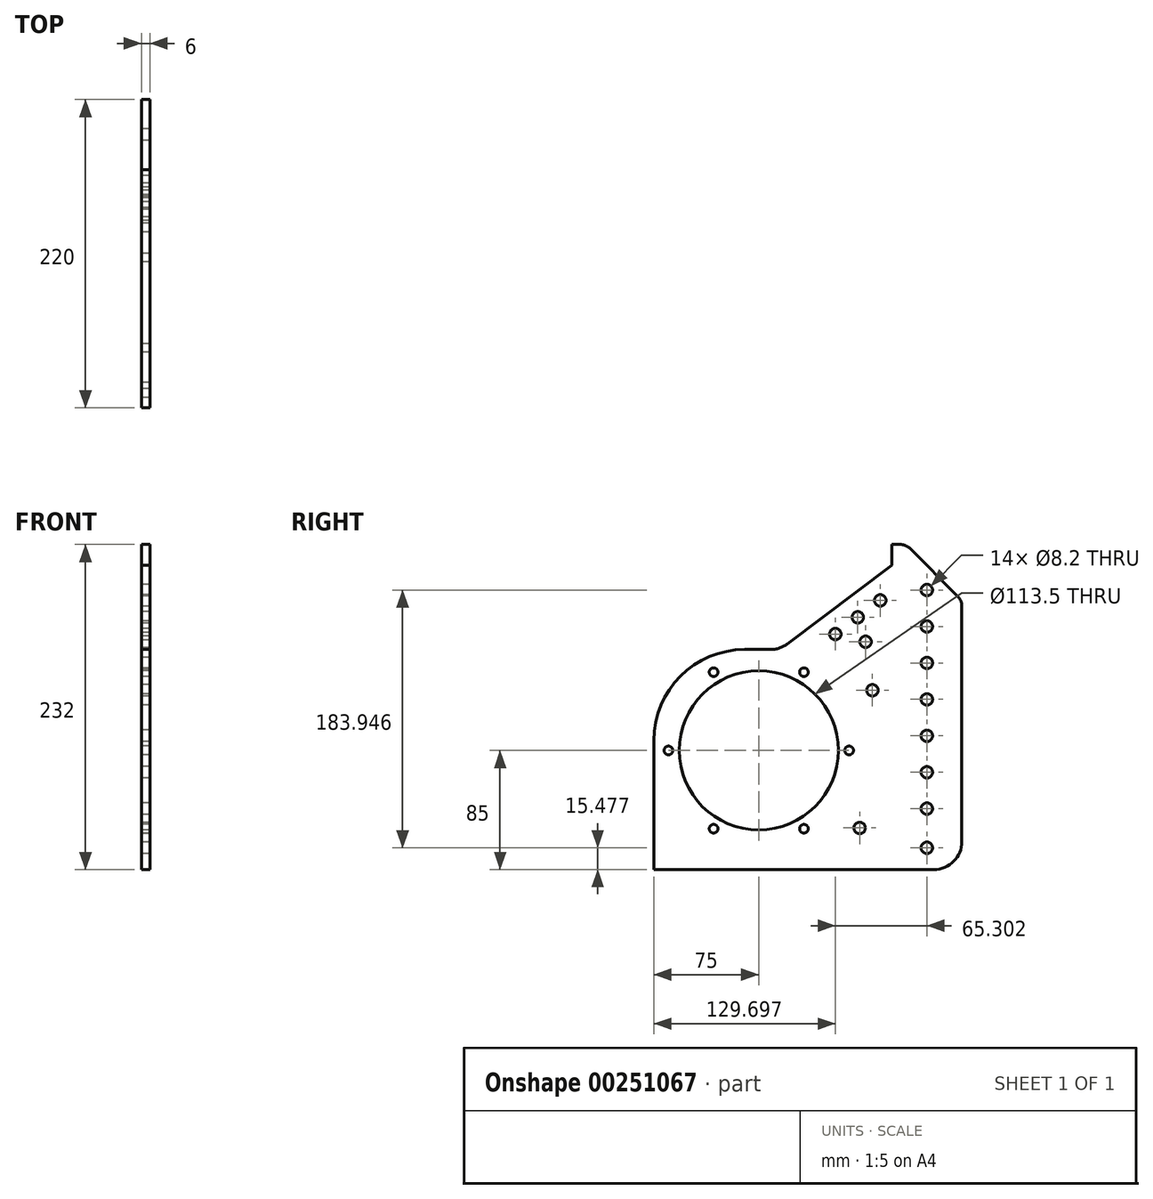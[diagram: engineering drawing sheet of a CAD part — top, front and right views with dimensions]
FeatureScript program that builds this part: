
annotation { "Feature Type Name" : "Feature", "Feature Type Description" : "" }
export const myFeature = defineFeature(function(context is Context, id is Id, definition is map)
    precondition{}
    {
        {
            var Q0;
            Q0=qCreatedBy(makeId("Right.planeOp"),FACE);
            var sketch = newSketch(context, id + "F0", { "sketchPlane" : qUnion([Q0])});
            skLineSegment(sketch, "E0.bottom", {"start": v(-20, 0) * mm, "end": v(-220, 0) * mm});
            skLineSegment(sketch, "E0.left", {"start": v(0, 20) * mm, "end": v(0, 187.86) * mm});
            skLineSegment(sketch, "E0.right", {"start": v(-220, 0) * mm, "end": v(-220, 92) * mm});
            skCircle(sketch, "E1", {"center": v(-145, 85) * mm, "radius": 56.75 * mm});
            skCircle(sketch, "E2", {"center": v(-145, 85) * mm, "radius": 64.5 * mm, "construction": true});
            skCircle(sketch, "E3", {"center": v(-80.5, 85) * mm, "radius": 3.1 * mm});
            skLineSegment(sketch, "E4", {"start": v(25.99, 85) * mm, "end": v(-259.94, 85) * mm, "construction": true});
            skCircle(sketch, "E5.1.0", {"center": v(-112.75, 140.86) * mm, "radius": 3.1 * mm});
            skCircle(sketch, "E5.2.0", {"center": v(-177.25, 140.86) * mm, "radius": 3.1 * mm});
            skCircle(sketch, "E5.3.0", {"center": v(-209.5, 85) * mm, "radius": 3.1 * mm});
            skCircle(sketch, "E5.4.0", {"center": v(-177.25, 29.14) * mm, "radius": 3.1 * mm});
            skCircle(sketch, "E5.5.0", {"center": v(-112.75, 29.14) * mm, "radius": 3.1 * mm});
            skCircle(sketch, "E6", {"center": v(-145, 85) * mm, "radius": 55 * mm, "construction": true});
            skCircle(sketch, "E7", {"center": v(-145, 85) * mm, "radius": 42.5 * mm, "construction": true});
            skLineSegment(sketch, "E8", {"start": v(-25, -2.5) * mm, "end": v(-25, 245.05) * mm, "construction": true});
            skLineSegment(sketch, "E9.top", {"start": v(-44.14, 232) * mm, "end": v(-50, 232) * mm});
            skLineSegment(sketch, "E9.right", {"start": v(-50, 157) * mm, "end": v(-50, 232) * mm});
            skCircle(sketch, "E10", {"center": v(-25, 199.42) * mm, "radius": 26 * mm, "construction": true});
            skCircle(sketch, "E11", {"center": v(-25, 199.42) * mm, "radius": 4.1 * mm});
            skLineSegment(sketch, "E12", {"start": v(-136.67, 157) * mm, "end": v(-155, 157) * mm});
            skLineSegment(sketch, "E13.bottom", {"start": v(-50, 232) * mm, "end": v(-44, 232) * mm, "construction": true});
            skLineSegment(sketch, "E13.top", {"start": v(-50, 0) * mm, "end": v(-44, 0) * mm, "construction": true});
            skLineSegment(sketch, "E13.left", {"start": v(-50, 232) * mm, "end": v(-50, 0) * mm, "construction": true});
            skLineSegment(sketch, "E13.right", {"start": v(-44, 232) * mm, "end": v(-44, 0) * mm, "construction": true});
            skCircle(sketch, "E14.0.1.0", {"center": v(-25, 173.42) * mm, "radius": 4.1 * mm});
            skCircle(sketch, "E14.0.2.0", {"center": v(-25, 147.42) * mm, "radius": 4.1 * mm});
            skCircle(sketch, "E14.0.3.0", {"center": v(-25, 121.42) * mm, "radius": 4.1 * mm});
            skCircle(sketch, "E14.0.4.0", {"center": v(-25, 95.42) * mm, "radius": 4.1 * mm});
            skCircle(sketch, "E14.0.5.0", {"center": v(-25, 69.42) * mm, "radius": 4.1 * mm});
            skCircle(sketch, "E14.0.6.0", {"center": v(-25, 43.42) * mm, "radius": 4.1 * mm});
            skCircle(sketch, "E14.0.7.0", {"center": v(-25, 15.48) * mm, "radius": 4.1 * mm});
            skLineSegment(sketch, "E14.direction2", {"start": v(-25, 199.42) * mm, "end": v(-25, 173.42) * mm, "construction": true});
            skPoint(sketch, "E15.visualSharp", {"position": v(0, 232) * mm});
            skPoint(sketch, "E16.visualSharp", {"position": v(0, 0) * mm});
            skArc(sketch, "E16.filletArc", {"start": v(-20, 0) * mm, "mid": v(-5.86, 5.86) * mm, "end": v(0, 20) * mm});
            skPoint(sketch, "E17.visualSharp", {"position": v(-220, 157) * mm});
            skArc(sketch, "E17.filletArc", {"start": v(-155, 157) * mm, "mid": v(-200.96, 137.96) * mm, "end": v(-220, 92) * mm});
            skPoint(sketch, "E18.visualSharp", {"position": v(-220, 0) * mm});
            skCircle(sketch, "E19", {"center": v(-72.99, 29.66) * mm, "radius": 4.1 * mm});
            skCircle(sketch, "E20", {"center": v(-63.87, 127.94) * mm, "radius": 4.1 * mm});
            skCircle(sketch, "E21", {"center": v(-63.87, 127.94) * mm, "radius": 20 * mm, "construction": true});
            skCircle(sketch, "E22", {"center": v(-72.99, 29.66) * mm, "radius": 26 * mm, "construction": true});
            skCircle(sketch, "E23", {"center": v(-25, 121.42) * mm, "radius": 26 * mm, "construction": true});
            skCircle(sketch, "E24", {"center": v(-25, 43.42) * mm, "radius": 26 * mm, "construction": true});
            skLineSegment(sketch, "E25", {"start": v(-2.93, 194.93) * mm, "end": v(-37.07, 229.07) * mm});
            skPoint(sketch, "E26.visualSharp", {"position": v(0, 192) * mm});
            skArc(sketch, "E26.filletArc", {"start": v(0, 187.86) * mm, "mid": v(-0.76, 191.68) * mm, "end": v(-2.93, 194.93) * mm});
            skPoint(sketch, "E27.visualSharp", {"position": v(-40, 232) * mm});
            skArc(sketch, "E27.filletArc", {"start": v(-37.07, 229.07) * mm, "mid": v(-40.32, 231.24) * mm, "end": v(-44.14, 232) * mm});
            skLineSegment(sketch, "E28", {"start": v(-50, 217) * mm, "end": v(-124.67, 161) * mm});
            skCircle(sketch, "E29", {"center": v(-58.3, 192.02) * mm, "radius": 26 * mm, "construction": true});
            skCircle(sketch, "E30", {"center": v(-58.3, 192.02) * mm, "radius": 4.1 * mm});
            skCircle(sketch, "E31", {"center": v(-74.3, 180.02) * mm, "radius": 4.1 * mm});
            skCircle(sketch, "E32", {"center": v(-90.3, 168.02) * mm, "radius": 4.1 * mm});
            skLineSegment(sketch, "E33", {"start": v(-107.79, 154.9) * mm, "end": v(-46.32, 201.01) * mm, "construction": true});
            skPoint(sketch, "E34.visualSharp", {"position": v(-130, 157) * mm});
            skArc(sketch, "E34.filletArc", {"start": v(-136.67, 157) * mm, "mid": v(-130.34, 158.03) * mm, "end": v(-124.67, 161) * mm});
            skCircle(sketch, "E35", {"center": v(-68.75, 162.53) * mm, "radius": 4.1 * mm});
            skSolve(sketch);
        }
        {
            var Q0;
            Q0 = qSketchRegion(id + "F0", true);
            extrude(context, id + "F1", {"entities" : qUnion([Q0]), "depth" : 6 * mm});
        }
    });
